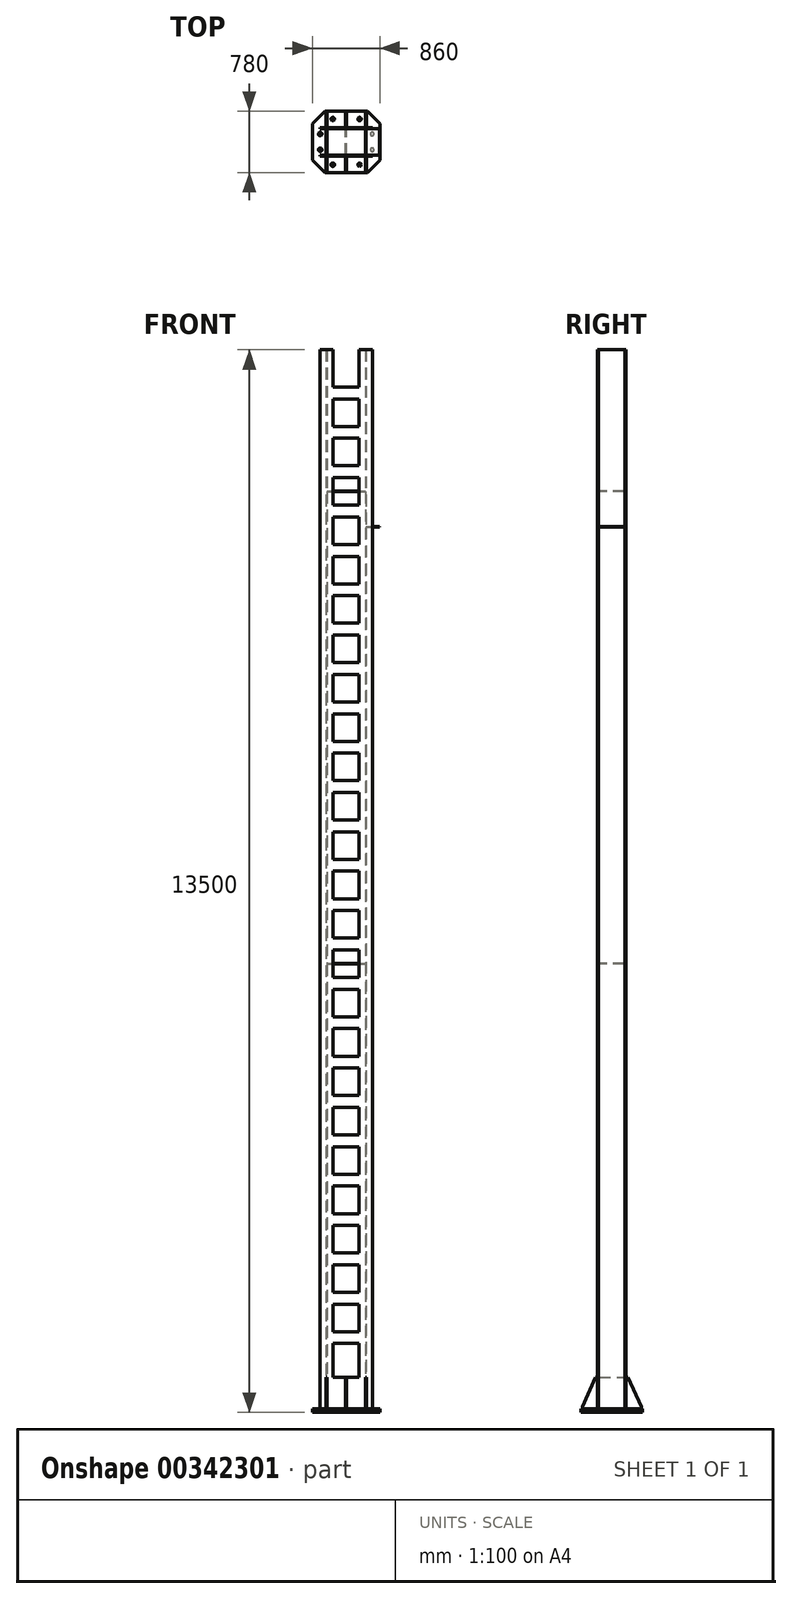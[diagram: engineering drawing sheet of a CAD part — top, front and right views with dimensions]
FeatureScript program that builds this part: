
annotation { "Feature Type Name" : "Feature", "Feature Type Description" : "" }
export const myFeature = defineFeature(function(context is Context, id is Id, definition is map)
    precondition{}
    {
        {
            var Q0;
            Q0=qCreatedBy(makeId("Top.planeOp"),FACE);
            var sketch = newSketch(context, id + "F0", { "sketchPlane" : qUnion([Q0])});
            skLineSegment(sketch, "E0", {"start": v(-335, 180) * mm, "end": v(335, 180) * mm});
            skLineSegment(sketch, "E1", {"start": v(335, 180) * mm, "end": v(335, 167.3) * mm});
            skLineSegment(sketch, "E2", {"start": v(335, 167.3) * mm, "end": v(254, 167.3) * mm});
            skLineSegment(sketch, "E3", {"start": v(254, 167.3) * mm, "end": v(254, -167.3) * mm});
            skLineSegment(sketch, "E4", {"start": v(254, -167.3) * mm, "end": v(335, -167.3) * mm});
            skLineSegment(sketch, "E5", {"start": v(335, -167.3) * mm, "end": v(335, -180) * mm});
            skLineSegment(sketch, "E6", {"start": v(335, -180) * mm, "end": v(-335, -180) * mm});
            skLineSegment(sketch, "E7", {"start": v(-335, -180) * mm, "end": v(-335, -167.3) * mm});
            skLineSegment(sketch, "E8", {"start": v(-335, -167.3) * mm, "end": v(-254, -167.3) * mm});
            skLineSegment(sketch, "E9", {"start": v(-254, -167.3) * mm, "end": v(-254, 167.3) * mm});
            skLineSegment(sketch, "E10", {"start": v(-254, 167.3) * mm, "end": v(-335, 167.3) * mm});
            skLineSegment(sketch, "E11", {"start": v(-335, 167.3) * mm, "end": v(-335, 180) * mm});
            skPoint(sketch, "E12.visualSharp", {"position": v(-254, 167.3) * mm});
            skPoint(sketch, "E13.visualSharp", {"position": v(254, 167.3) * mm});
            skPoint(sketch, "E14.visualSharp", {"position": v(254, -167.3) * mm});
            skPoint(sketch, "E15.visualSharp", {"position": v(-254, -167.3) * mm});
            skSolve(sketch);
        }
        {
            var Q0;
            Q0=qSketchRegion(id+"F0",true);
            extrude(context, id + "F1", {"entities" : qUnion([Q0]), "depth" : 13500 * mm});
        }
        {
            var Q0;
            Q0=makeQuery(id+"F1.opExtrude","CAP_FACE",FACE,{"disambiguationData":[OSD([sQuery(id+"F0.wireOp",EDGE,"E0"),sQuery(id+"F0.wireOp",EDGE,"E1"),sQuery(id+"F0.wireOp",EDGE,"E2"),sQuery(id+"F0.wireOp",EDGE,"E3"),sQuery(id+"F0.wireOp",EDGE,"E4"),sQuery(id+"F0.wireOp",EDGE,"E5"),sQuery(id+"F0.wireOp",EDGE,"E6"),sQuery(id+"F0.wireOp",EDGE,"E7"),sQuery(id+"F0.wireOp",EDGE,"E8"),sQuery(id+"F0.wireOp",EDGE,"E9"),sQuery(id+"F0.wireOp",EDGE,"E10"),sQuery(id+"F0.wireOp",EDGE,"E11"),sQuery(id+"F0.wireOp",EDGE,"E12.filletArc"),sQuery(id+"F0.wireOp",EDGE,"E13.filletArc"),sQuery(id+"F0.wireOp",EDGE,"E14.filletArc"),sQuery(id+"F0.wireOp",EDGE,"E15.filletArc")])],"isStart":true});
            var sketch = newSketch(context, id + "F2", { "sketchPlane" : qUnion([Q0])});
            skLineSegment(sketch, "E16.bottom", {"start": v(-246, 167.3) * mm, "end": v(246, 167.3) * mm});
            skLineSegment(sketch, "E16.top", {"start": v(-246, -167.3) * mm, "end": v(246, -167.3) * mm});
            skLineSegment(sketch, "E16.left", {"start": v(-246, 167.3) * mm, "end": v(-246, -167.3) * mm});
            skLineSegment(sketch, "E16.right", {"start": v(246, 167.3) * mm, "end": v(246, -167.3) * mm});
            skPoint(sketch, "E17.visualSharp", {"position": v(-246, 167.3) * mm});
            skPoint(sketch, "E18.visualSharp", {"position": v(246, 167.3) * mm});
            skPoint(sketch, "E19.visualSharp", {"position": v(246, -167.3) * mm});
            skPoint(sketch, "E20.visualSharp", {"position": v(-246, -167.3) * mm});
            skLineSegment(sketch, "E21", {"start": v(-272.18, 0) * mm, "end": v(268.26, 0) * mm, "construction": true});
            skLineSegment(sketch, "E22", {"start": v(0, 198) * mm, "end": v(0, -205.98) * mm, "construction": true});
            skSolve(sketch);
        }
        {
            var Q0;
            Q0=qSketchRegion(id+"F2",true);
            extrude(context, id + "F3", {"entities" : qUnion([Q0]), "operationType" : NewBodyOperationType.REMOVE, "endBound" : BoundingType.THROUGH_ALL, "oppositeDirection" : true, "depth" : 25.4 * mm});
        }
        {
            var Q0;
            Q0=makeQuery(id+"F1.opExtrude","SWEPT_FACE",FACE,{"disambiguationData":[OSD([sQuery(id+"F0.wireOp",EDGE,"E6")])]});
            var sketch = newSketch(context, id + "F4", { "sketchPlane" : qUnion([Q0])});
            skLineSegment(sketch, "E23.bottom", {"start": v(-165, 1375) * mm, "end": v(165, 1375) * mm});
            skLineSegment(sketch, "E23.top", {"start": v(-165, 1025) * mm, "end": v(165, 1025) * mm});
            skLineSegment(sketch, "E23.left", {"start": v(-165, 1375) * mm, "end": v(-165, 1025) * mm});
            skLineSegment(sketch, "E23.right", {"start": v(165, 1375) * mm, "end": v(165, 1025) * mm});
            skLineSegment(sketch, "E24", {"start": v(0, -2627.58) * mm, "end": v(0, 406140.36) * mm, "construction": true});
            skLineSegment(sketch, "E25.0.1.0", {"start": v(-165, 1875) * mm, "end": v(165, 1875) * mm});
            skLineSegment(sketch, "E25.0.1.1", {"start": v(-165, 1525) * mm, "end": v(165, 1525) * mm});
            skLineSegment(sketch, "E25.0.1.2", {"start": v(-165, 1875) * mm, "end": v(-165, 1525) * mm});
            skLineSegment(sketch, "E25.0.1.3", {"start": v(165, 1875) * mm, "end": v(165, 1525) * mm});
            skLineSegment(sketch, "E25.0.2.0", {"start": v(-165, 2375) * mm, "end": v(165, 2375) * mm});
            skLineSegment(sketch, "E25.0.2.1", {"start": v(-165, 2025) * mm, "end": v(165, 2025) * mm});
            skLineSegment(sketch, "E25.0.2.2", {"start": v(-165, 2375) * mm, "end": v(-165, 2025) * mm});
            skLineSegment(sketch, "E25.0.2.3", {"start": v(165, 2375) * mm, "end": v(165, 2025) * mm});
            skLineSegment(sketch, "E25.0.3.0", {"start": v(-165, 2875) * mm, "end": v(165, 2875) * mm});
            skLineSegment(sketch, "E25.0.3.1", {"start": v(-165, 2525) * mm, "end": v(165, 2525) * mm});
            skLineSegment(sketch, "E25.0.3.2", {"start": v(-165, 2875) * mm, "end": v(-165, 2525) * mm});
            skLineSegment(sketch, "E25.0.3.3", {"start": v(165, 2875) * mm, "end": v(165, 2525) * mm});
            skLineSegment(sketch, "E25.0.4.0", {"start": v(-165, 3375) * mm, "end": v(165, 3375) * mm});
            skLineSegment(sketch, "E25.0.4.1", {"start": v(-165, 3025) * mm, "end": v(165, 3025) * mm});
            skLineSegment(sketch, "E25.0.4.2", {"start": v(-165, 3375) * mm, "end": v(-165, 3025) * mm});
            skLineSegment(sketch, "E25.0.4.3", {"start": v(165, 3375) * mm, "end": v(165, 3025) * mm});
            skLineSegment(sketch, "E25.0.5.0", {"start": v(-165, 3875) * mm, "end": v(165, 3875) * mm});
            skLineSegment(sketch, "E25.0.5.1", {"start": v(-165, 3525) * mm, "end": v(165, 3525) * mm});
            skLineSegment(sketch, "E25.0.5.2", {"start": v(-165, 3875) * mm, "end": v(-165, 3525) * mm});
            skLineSegment(sketch, "E25.0.5.3", {"start": v(165, 3875) * mm, "end": v(165, 3525) * mm});
            skLineSegment(sketch, "E25.0.6.0", {"start": v(-165, 4375) * mm, "end": v(165, 4375) * mm});
            skLineSegment(sketch, "E25.0.6.1", {"start": v(-165, 4025) * mm, "end": v(165, 4025) * mm});
            skLineSegment(sketch, "E25.0.6.2", {"start": v(-165, 4375) * mm, "end": v(-165, 4025) * mm});
            skLineSegment(sketch, "E25.0.6.3", {"start": v(165, 4375) * mm, "end": v(165, 4025) * mm});
            skLineSegment(sketch, "E25.0.7.0", {"start": v(-165, 4875) * mm, "end": v(165, 4875) * mm});
            skLineSegment(sketch, "E25.0.7.1", {"start": v(-165, 4525) * mm, "end": v(165, 4525) * mm});
            skLineSegment(sketch, "E25.0.7.2", {"start": v(-165, 4875) * mm, "end": v(-165, 4525) * mm});
            skLineSegment(sketch, "E25.0.7.3", {"start": v(165, 4875) * mm, "end": v(165, 4525) * mm});
            skLineSegment(sketch, "E25.0.8.0", {"start": v(-165, 5375) * mm, "end": v(165, 5375) * mm});
            skLineSegment(sketch, "E25.0.8.1", {"start": v(-165, 5025) * mm, "end": v(165, 5025) * mm});
            skLineSegment(sketch, "E25.0.8.2", {"start": v(-165, 5375) * mm, "end": v(-165, 5025) * mm});
            skLineSegment(sketch, "E25.0.8.3", {"start": v(165, 5375) * mm, "end": v(165, 5025) * mm});
            skLineSegment(sketch, "E25.0.9.0", {"start": v(-165, 5875) * mm, "end": v(165, 5875) * mm});
            skLineSegment(sketch, "E25.0.9.1", {"start": v(-165, 5525) * mm, "end": v(165, 5525) * mm});
            skLineSegment(sketch, "E25.0.9.2", {"start": v(-165, 5875) * mm, "end": v(-165, 5525) * mm});
            skLineSegment(sketch, "E25.0.9.3", {"start": v(165, 5875) * mm, "end": v(165, 5525) * mm});
            skLineSegment(sketch, "E25.0.10.0", {"start": v(-165, 6375) * mm, "end": v(165, 6375) * mm});
            skLineSegment(sketch, "E25.0.10.1", {"start": v(-165, 6025) * mm, "end": v(165, 6025) * mm});
            skLineSegment(sketch, "E25.0.10.2", {"start": v(-165, 6375) * mm, "end": v(-165, 6025) * mm});
            skLineSegment(sketch, "E25.0.10.3", {"start": v(165, 6375) * mm, "end": v(165, 6025) * mm});
            skLineSegment(sketch, "E25.0.11.0", {"start": v(-165, 6875) * mm, "end": v(165, 6875) * mm});
            skLineSegment(sketch, "E25.0.11.1", {"start": v(-165, 6525) * mm, "end": v(165, 6525) * mm});
            skLineSegment(sketch, "E25.0.11.2", {"start": v(-165, 6875) * mm, "end": v(-165, 6525) * mm});
            skLineSegment(sketch, "E25.0.11.3", {"start": v(165, 6875) * mm, "end": v(165, 6525) * mm});
            skLineSegment(sketch, "E25.0.12.0", {"start": v(-165, 7375) * mm, "end": v(165, 7375) * mm});
            skLineSegment(sketch, "E25.0.12.1", {"start": v(-165, 7025) * mm, "end": v(165, 7025) * mm});
            skLineSegment(sketch, "E25.0.12.2", {"start": v(-165, 7375) * mm, "end": v(-165, 7025) * mm});
            skLineSegment(sketch, "E25.0.12.3", {"start": v(165, 7375) * mm, "end": v(165, 7025) * mm});
            skLineSegment(sketch, "E25.0.13.0", {"start": v(-165, 7875) * mm, "end": v(165, 7875) * mm});
            skLineSegment(sketch, "E25.0.13.1", {"start": v(-165, 7525) * mm, "end": v(165, 7525) * mm});
            skLineSegment(sketch, "E25.0.13.2", {"start": v(-165, 7875) * mm, "end": v(-165, 7525) * mm});
            skLineSegment(sketch, "E25.0.13.3", {"start": v(165, 7875) * mm, "end": v(165, 7525) * mm});
            skLineSegment(sketch, "E25.0.14.0", {"start": v(-165, 8375) * mm, "end": v(165, 8375) * mm});
            skLineSegment(sketch, "E25.0.14.1", {"start": v(-165, 8025) * mm, "end": v(165, 8025) * mm});
            skLineSegment(sketch, "E25.0.14.2", {"start": v(-165, 8375) * mm, "end": v(-165, 8025) * mm});
            skLineSegment(sketch, "E25.0.14.3", {"start": v(165, 8375) * mm, "end": v(165, 8025) * mm});
            skLineSegment(sketch, "E25.0.15.0", {"start": v(-165, 8875) * mm, "end": v(165, 8875) * mm});
            skLineSegment(sketch, "E25.0.15.1", {"start": v(-165, 8525) * mm, "end": v(165, 8525) * mm});
            skLineSegment(sketch, "E25.0.15.2", {"start": v(-165, 8875) * mm, "end": v(-165, 8525) * mm});
            skLineSegment(sketch, "E25.0.15.3", {"start": v(165, 8875) * mm, "end": v(165, 8525) * mm});
            skLineSegment(sketch, "E25.0.16.0", {"start": v(-165, 9375) * mm, "end": v(165, 9375) * mm});
            skLineSegment(sketch, "E25.0.16.1", {"start": v(-165, 9025) * mm, "end": v(165, 9025) * mm});
            skLineSegment(sketch, "E25.0.16.2", {"start": v(-165, 9375) * mm, "end": v(-165, 9025) * mm});
            skLineSegment(sketch, "E25.0.16.3", {"start": v(165, 9375) * mm, "end": v(165, 9025) * mm});
            skLineSegment(sketch, "E25.0.17.0", {"start": v(-165, 9875) * mm, "end": v(165, 9875) * mm});
            skLineSegment(sketch, "E25.0.17.1", {"start": v(-165, 9525) * mm, "end": v(165, 9525) * mm});
            skLineSegment(sketch, "E25.0.17.2", {"start": v(-165, 9875) * mm, "end": v(-165, 9525) * mm});
            skLineSegment(sketch, "E25.0.17.3", {"start": v(165, 9875) * mm, "end": v(165, 9525) * mm});
            skLineSegment(sketch, "E25.0.18.0", {"start": v(-165, 10375) * mm, "end": v(165, 10375) * mm});
            skLineSegment(sketch, "E25.0.18.1", {"start": v(-165, 10025) * mm, "end": v(165, 10025) * mm});
            skLineSegment(sketch, "E25.0.18.2", {"start": v(-165, 10375) * mm, "end": v(-165, 10025) * mm});
            skLineSegment(sketch, "E25.0.18.3", {"start": v(165, 10375) * mm, "end": v(165, 10025) * mm});
            skLineSegment(sketch, "E25.0.19.0", {"start": v(-165, 10875) * mm, "end": v(165, 10875) * mm});
            skLineSegment(sketch, "E25.0.19.1", {"start": v(-165, 10525) * mm, "end": v(165, 10525) * mm});
            skLineSegment(sketch, "E25.0.19.2", {"start": v(-165, 10875) * mm, "end": v(-165, 10525) * mm});
            skLineSegment(sketch, "E25.0.19.3", {"start": v(165, 10875) * mm, "end": v(165, 10525) * mm});
            skLineSegment(sketch, "E25.0.20.0", {"start": v(-165, 11375) * mm, "end": v(165, 11375) * mm});
            skLineSegment(sketch, "E25.0.20.1", {"start": v(-165, 11025) * mm, "end": v(165, 11025) * mm});
            skLineSegment(sketch, "E25.0.20.2", {"start": v(-165, 11375) * mm, "end": v(-165, 11025) * mm});
            skLineSegment(sketch, "E25.0.20.3", {"start": v(165, 11375) * mm, "end": v(165, 11025) * mm});
            skLineSegment(sketch, "E25.0.21.0", {"start": v(-165, 11875) * mm, "end": v(165, 11875) * mm});
            skLineSegment(sketch, "E25.0.21.1", {"start": v(-165, 11525) * mm, "end": v(165, 11525) * mm});
            skLineSegment(sketch, "E25.0.21.2", {"start": v(-165, 11875) * mm, "end": v(-165, 11525) * mm});
            skLineSegment(sketch, "E25.0.21.3", {"start": v(165, 11875) * mm, "end": v(165, 11525) * mm});
            skLineSegment(sketch, "E25.0.22.0", {"start": v(-165, 12375) * mm, "end": v(165, 12375) * mm});
            skLineSegment(sketch, "E25.0.22.1", {"start": v(-165, 12025) * mm, "end": v(165, 12025) * mm});
            skLineSegment(sketch, "E25.0.22.2", {"start": v(-165, 12375) * mm, "end": v(-165, 12025) * mm});
            skLineSegment(sketch, "E25.0.22.3", {"start": v(165, 12375) * mm, "end": v(165, 12025) * mm});
            skLineSegment(sketch, "E25.0.23.0", {"start": v(-165, 12875) * mm, "end": v(165, 12875) * mm});
            skLineSegment(sketch, "E25.0.23.1", {"start": v(-165, 12525) * mm, "end": v(165, 12525) * mm});
            skLineSegment(sketch, "E25.0.23.2", {"start": v(-165, 12875) * mm, "end": v(-165, 12525) * mm});
            skLineSegment(sketch, "E25.0.23.3", {"start": v(165, 12875) * mm, "end": v(165, 12525) * mm});
            skLineSegment(sketch, "E25.1.1.0", {"start": v(-165, 1875) * mm, "end": v(165, 1875) * mm});
            skLineSegment(sketch, "E25.1.1.1", {"start": v(-165, 1525) * mm, "end": v(165, 1525) * mm});
            skLineSegment(sketch, "E25.1.1.2", {"start": v(-165, 1875) * mm, "end": v(-165, 1525) * mm});
            skLineSegment(sketch, "E25.1.1.3", {"start": v(165, 1875) * mm, "end": v(165, 1525) * mm});
            skLineSegment(sketch, "E25.1.2.0", {"start": v(-165, 2375) * mm, "end": v(165, 2375) * mm});
            skLineSegment(sketch, "E25.1.2.1", {"start": v(-165, 2025) * mm, "end": v(165, 2025) * mm});
            skLineSegment(sketch, "E25.1.2.2", {"start": v(-165, 2375) * mm, "end": v(-165, 2025) * mm});
            skLineSegment(sketch, "E25.1.2.3", {"start": v(165, 2375) * mm, "end": v(165, 2025) * mm});
            skLineSegment(sketch, "E25.1.3.0", {"start": v(-165, 2875) * mm, "end": v(165, 2875) * mm});
            skLineSegment(sketch, "E25.1.3.1", {"start": v(-165, 2525) * mm, "end": v(165, 2525) * mm});
            skLineSegment(sketch, "E25.1.3.2", {"start": v(-165, 2875) * mm, "end": v(-165, 2525) * mm});
            skLineSegment(sketch, "E25.1.3.3", {"start": v(165, 2875) * mm, "end": v(165, 2525) * mm});
            skLineSegment(sketch, "E25.1.4.0", {"start": v(-165, 3375) * mm, "end": v(165, 3375) * mm});
            skLineSegment(sketch, "E25.1.4.1", {"start": v(-165, 3025) * mm, "end": v(165, 3025) * mm});
            skLineSegment(sketch, "E25.1.4.2", {"start": v(-165, 3375) * mm, "end": v(-165, 3025) * mm});
            skLineSegment(sketch, "E25.1.4.3", {"start": v(165, 3375) * mm, "end": v(165, 3025) * mm});
            skLineSegment(sketch, "E25.1.5.0", {"start": v(-165, 3875) * mm, "end": v(165, 3875) * mm});
            skLineSegment(sketch, "E25.1.5.1", {"start": v(-165, 3525) * mm, "end": v(165, 3525) * mm});
            skLineSegment(sketch, "E25.1.5.2", {"start": v(-165, 3875) * mm, "end": v(-165, 3525) * mm});
            skLineSegment(sketch, "E25.1.5.3", {"start": v(165, 3875) * mm, "end": v(165, 3525) * mm});
            skLineSegment(sketch, "E25.1.6.0", {"start": v(-165, 4375) * mm, "end": v(165, 4375) * mm});
            skLineSegment(sketch, "E25.1.6.1", {"start": v(-165, 4025) * mm, "end": v(165, 4025) * mm});
            skLineSegment(sketch, "E25.1.6.2", {"start": v(-165, 4375) * mm, "end": v(-165, 4025) * mm});
            skLineSegment(sketch, "E25.1.6.3", {"start": v(165, 4375) * mm, "end": v(165, 4025) * mm});
            skLineSegment(sketch, "E25.1.7.0", {"start": v(-165, 4875) * mm, "end": v(165, 4875) * mm});
            skLineSegment(sketch, "E25.1.7.1", {"start": v(-165, 4525) * mm, "end": v(165, 4525) * mm});
            skLineSegment(sketch, "E25.1.7.2", {"start": v(-165, 4875) * mm, "end": v(-165, 4525) * mm});
            skLineSegment(sketch, "E25.1.7.3", {"start": v(165, 4875) * mm, "end": v(165, 4525) * mm});
            skLineSegment(sketch, "E25.1.8.0", {"start": v(-165, 5375) * mm, "end": v(165, 5375) * mm});
            skLineSegment(sketch, "E25.1.8.1", {"start": v(-165, 5025) * mm, "end": v(165, 5025) * mm});
            skLineSegment(sketch, "E25.1.8.2", {"start": v(-165, 5375) * mm, "end": v(-165, 5025) * mm});
            skLineSegment(sketch, "E25.1.8.3", {"start": v(165, 5375) * mm, "end": v(165, 5025) * mm});
            skLineSegment(sketch, "E25.1.9.0", {"start": v(-165, 5875) * mm, "end": v(165, 5875) * mm});
            skLineSegment(sketch, "E25.1.9.1", {"start": v(-165, 5525) * mm, "end": v(165, 5525) * mm});
            skLineSegment(sketch, "E25.1.9.2", {"start": v(-165, 5875) * mm, "end": v(-165, 5525) * mm});
            skLineSegment(sketch, "E25.1.9.3", {"start": v(165, 5875) * mm, "end": v(165, 5525) * mm});
            skLineSegment(sketch, "E25.1.10.0", {"start": v(-165, 6375) * mm, "end": v(165, 6375) * mm});
            skLineSegment(sketch, "E25.1.10.1", {"start": v(-165, 6025) * mm, "end": v(165, 6025) * mm});
            skLineSegment(sketch, "E25.1.10.2", {"start": v(-165, 6375) * mm, "end": v(-165, 6025) * mm});
            skLineSegment(sketch, "E25.1.10.3", {"start": v(165, 6375) * mm, "end": v(165, 6025) * mm});
            skLineSegment(sketch, "E25.1.11.0", {"start": v(-165, 6875) * mm, "end": v(165, 6875) * mm});
            skLineSegment(sketch, "E25.1.11.1", {"start": v(-165, 6525) * mm, "end": v(165, 6525) * mm});
            skLineSegment(sketch, "E25.1.11.2", {"start": v(-165, 6875) * mm, "end": v(-165, 6525) * mm});
            skLineSegment(sketch, "E25.1.11.3", {"start": v(165, 6875) * mm, "end": v(165, 6525) * mm});
            skLineSegment(sketch, "E25.1.12.0", {"start": v(-165, 7375) * mm, "end": v(165, 7375) * mm});
            skLineSegment(sketch, "E25.1.12.1", {"start": v(-165, 7025) * mm, "end": v(165, 7025) * mm});
            skLineSegment(sketch, "E25.1.12.2", {"start": v(-165, 7375) * mm, "end": v(-165, 7025) * mm});
            skLineSegment(sketch, "E25.1.12.3", {"start": v(165, 7375) * mm, "end": v(165, 7025) * mm});
            skLineSegment(sketch, "E25.1.13.0", {"start": v(-165, 7875) * mm, "end": v(165, 7875) * mm});
            skLineSegment(sketch, "E25.1.13.1", {"start": v(-165, 7525) * mm, "end": v(165, 7525) * mm});
            skLineSegment(sketch, "E25.1.13.2", {"start": v(-165, 7875) * mm, "end": v(-165, 7525) * mm});
            skLineSegment(sketch, "E25.1.13.3", {"start": v(165, 7875) * mm, "end": v(165, 7525) * mm});
            skLineSegment(sketch, "E25.1.14.0", {"start": v(-165, 8375) * mm, "end": v(165, 8375) * mm});
            skLineSegment(sketch, "E25.1.14.1", {"start": v(-165, 8025) * mm, "end": v(165, 8025) * mm});
            skLineSegment(sketch, "E25.1.14.2", {"start": v(-165, 8375) * mm, "end": v(-165, 8025) * mm});
            skLineSegment(sketch, "E25.1.14.3", {"start": v(165, 8375) * mm, "end": v(165, 8025) * mm});
            skLineSegment(sketch, "E25.1.15.0", {"start": v(-165, 8875) * mm, "end": v(165, 8875) * mm});
            skLineSegment(sketch, "E25.1.15.1", {"start": v(-165, 8525) * mm, "end": v(165, 8525) * mm});
            skLineSegment(sketch, "E25.1.15.2", {"start": v(-165, 8875) * mm, "end": v(-165, 8525) * mm});
            skLineSegment(sketch, "E25.1.15.3", {"start": v(165, 8875) * mm, "end": v(165, 8525) * mm});
            skLineSegment(sketch, "E25.1.16.0", {"start": v(-165, 9375) * mm, "end": v(165, 9375) * mm});
            skLineSegment(sketch, "E25.1.16.1", {"start": v(-165, 9025) * mm, "end": v(165, 9025) * mm});
            skLineSegment(sketch, "E25.1.16.2", {"start": v(-165, 9375) * mm, "end": v(-165, 9025) * mm});
            skLineSegment(sketch, "E25.1.16.3", {"start": v(165, 9375) * mm, "end": v(165, 9025) * mm});
            skLineSegment(sketch, "E25.1.17.0", {"start": v(-165, 9875) * mm, "end": v(165, 9875) * mm});
            skLineSegment(sketch, "E25.1.17.1", {"start": v(-165, 9525) * mm, "end": v(165, 9525) * mm});
            skLineSegment(sketch, "E25.1.17.2", {"start": v(-165, 9875) * mm, "end": v(-165, 9525) * mm});
            skLineSegment(sketch, "E25.1.17.3", {"start": v(165, 9875) * mm, "end": v(165, 9525) * mm});
            skLineSegment(sketch, "E25.1.18.0", {"start": v(-165, 10375) * mm, "end": v(165, 10375) * mm});
            skLineSegment(sketch, "E25.1.18.1", {"start": v(-165, 10025) * mm, "end": v(165, 10025) * mm});
            skLineSegment(sketch, "E25.1.18.2", {"start": v(-165, 10375) * mm, "end": v(-165, 10025) * mm});
            skLineSegment(sketch, "E25.1.18.3", {"start": v(165, 10375) * mm, "end": v(165, 10025) * mm});
            skLineSegment(sketch, "E25.1.19.0", {"start": v(-165, 10875) * mm, "end": v(165, 10875) * mm});
            skLineSegment(sketch, "E25.1.19.1", {"start": v(-165, 10525) * mm, "end": v(165, 10525) * mm});
            skLineSegment(sketch, "E25.1.19.2", {"start": v(-165, 10875) * mm, "end": v(-165, 10525) * mm});
            skLineSegment(sketch, "E25.1.19.3", {"start": v(165, 10875) * mm, "end": v(165, 10525) * mm});
            skLineSegment(sketch, "E25.1.20.0", {"start": v(-165, 11375) * mm, "end": v(165, 11375) * mm});
            skLineSegment(sketch, "E25.1.20.1", {"start": v(-165, 11025) * mm, "end": v(165, 11025) * mm});
            skLineSegment(sketch, "E25.1.20.2", {"start": v(-165, 11375) * mm, "end": v(-165, 11025) * mm});
            skLineSegment(sketch, "E25.1.20.3", {"start": v(165, 11375) * mm, "end": v(165, 11025) * mm});
            skLineSegment(sketch, "E25.1.21.0", {"start": v(-165, 11875) * mm, "end": v(165, 11875) * mm});
            skLineSegment(sketch, "E25.1.21.1", {"start": v(-165, 11525) * mm, "end": v(165, 11525) * mm});
            skLineSegment(sketch, "E25.1.21.2", {"start": v(-165, 11875) * mm, "end": v(-165, 11525) * mm});
            skLineSegment(sketch, "E25.1.21.3", {"start": v(165, 11875) * mm, "end": v(165, 11525) * mm});
            skLineSegment(sketch, "E25.1.22.0", {"start": v(-165, 12375) * mm, "end": v(165, 12375) * mm});
            skLineSegment(sketch, "E25.1.22.1", {"start": v(-165, 12025) * mm, "end": v(165, 12025) * mm});
            skLineSegment(sketch, "E25.1.22.2", {"start": v(-165, 12375) * mm, "end": v(-165, 12025) * mm});
            skLineSegment(sketch, "E25.1.22.3", {"start": v(165, 12375) * mm, "end": v(165, 12025) * mm});
            skLineSegment(sketch, "E25.1.23.0", {"start": v(-165, 12875) * mm, "end": v(165, 12875) * mm});
            skLineSegment(sketch, "E25.1.23.1", {"start": v(-165, 12525) * mm, "end": v(165, 12525) * mm});
            skLineSegment(sketch, "E25.1.23.2", {"start": v(-165, 12875) * mm, "end": v(-165, 12525) * mm});
            skLineSegment(sketch, "E25.1.23.3", {"start": v(165, 12875) * mm, "end": v(165, 12525) * mm});
            skLineSegment(sketch, "E25.2.1.0", {"start": v(-165, 1875) * mm, "end": v(165, 1875) * mm});
            skLineSegment(sketch, "E25.2.1.1", {"start": v(-165, 1525) * mm, "end": v(165, 1525) * mm});
            skLineSegment(sketch, "E25.2.1.2", {"start": v(-165, 1875) * mm, "end": v(-165, 1525) * mm});
            skLineSegment(sketch, "E25.2.1.3", {"start": v(165, 1875) * mm, "end": v(165, 1525) * mm});
            skLineSegment(sketch, "E25.2.2.0", {"start": v(-165, 2375) * mm, "end": v(165, 2375) * mm});
            skLineSegment(sketch, "E25.2.2.1", {"start": v(-165, 2025) * mm, "end": v(165, 2025) * mm});
            skLineSegment(sketch, "E25.2.2.2", {"start": v(-165, 2375) * mm, "end": v(-165, 2025) * mm});
            skLineSegment(sketch, "E25.2.2.3", {"start": v(165, 2375) * mm, "end": v(165, 2025) * mm});
            skLineSegment(sketch, "E25.2.3.0", {"start": v(-165, 2875) * mm, "end": v(165, 2875) * mm});
            skLineSegment(sketch, "E25.2.3.1", {"start": v(-165, 2525) * mm, "end": v(165, 2525) * mm});
            skLineSegment(sketch, "E25.2.3.2", {"start": v(-165, 2875) * mm, "end": v(-165, 2525) * mm});
            skLineSegment(sketch, "E25.2.3.3", {"start": v(165, 2875) * mm, "end": v(165, 2525) * mm});
            skLineSegment(sketch, "E25.2.4.0", {"start": v(-165, 3375) * mm, "end": v(165, 3375) * mm});
            skLineSegment(sketch, "E25.2.4.1", {"start": v(-165, 3025) * mm, "end": v(165, 3025) * mm});
            skLineSegment(sketch, "E25.2.4.2", {"start": v(-165, 3375) * mm, "end": v(-165, 3025) * mm});
            skLineSegment(sketch, "E25.2.4.3", {"start": v(165, 3375) * mm, "end": v(165, 3025) * mm});
            skLineSegment(sketch, "E25.2.5.0", {"start": v(-165, 3875) * mm, "end": v(165, 3875) * mm});
            skLineSegment(sketch, "E25.2.5.1", {"start": v(-165, 3525) * mm, "end": v(165, 3525) * mm});
            skLineSegment(sketch, "E25.2.5.2", {"start": v(-165, 3875) * mm, "end": v(-165, 3525) * mm});
            skLineSegment(sketch, "E25.2.5.3", {"start": v(165, 3875) * mm, "end": v(165, 3525) * mm});
            skLineSegment(sketch, "E25.2.6.0", {"start": v(-165, 4375) * mm, "end": v(165, 4375) * mm});
            skLineSegment(sketch, "E25.2.6.1", {"start": v(-165, 4025) * mm, "end": v(165, 4025) * mm});
            skLineSegment(sketch, "E25.2.6.2", {"start": v(-165, 4375) * mm, "end": v(-165, 4025) * mm});
            skLineSegment(sketch, "E25.2.6.3", {"start": v(165, 4375) * mm, "end": v(165, 4025) * mm});
            skLineSegment(sketch, "E25.2.7.0", {"start": v(-165, 4875) * mm, "end": v(165, 4875) * mm});
            skLineSegment(sketch, "E25.2.7.1", {"start": v(-165, 4525) * mm, "end": v(165, 4525) * mm});
            skLineSegment(sketch, "E25.2.7.2", {"start": v(-165, 4875) * mm, "end": v(-165, 4525) * mm});
            skLineSegment(sketch, "E25.2.7.3", {"start": v(165, 4875) * mm, "end": v(165, 4525) * mm});
            skLineSegment(sketch, "E25.2.8.0", {"start": v(-165, 5375) * mm, "end": v(165, 5375) * mm});
            skLineSegment(sketch, "E25.2.8.1", {"start": v(-165, 5025) * mm, "end": v(165, 5025) * mm});
            skLineSegment(sketch, "E25.2.8.2", {"start": v(-165, 5375) * mm, "end": v(-165, 5025) * mm});
            skLineSegment(sketch, "E25.2.8.3", {"start": v(165, 5375) * mm, "end": v(165, 5025) * mm});
            skLineSegment(sketch, "E25.2.9.0", {"start": v(-165, 5875) * mm, "end": v(165, 5875) * mm});
            skLineSegment(sketch, "E25.2.9.1", {"start": v(-165, 5525) * mm, "end": v(165, 5525) * mm});
            skLineSegment(sketch, "E25.2.9.2", {"start": v(-165, 5875) * mm, "end": v(-165, 5525) * mm});
            skLineSegment(sketch, "E25.2.9.3", {"start": v(165, 5875) * mm, "end": v(165, 5525) * mm});
            skLineSegment(sketch, "E25.2.10.0", {"start": v(-165, 6375) * mm, "end": v(165, 6375) * mm});
            skLineSegment(sketch, "E25.2.10.1", {"start": v(-165, 6025) * mm, "end": v(165, 6025) * mm});
            skLineSegment(sketch, "E25.2.10.2", {"start": v(-165, 6375) * mm, "end": v(-165, 6025) * mm});
            skLineSegment(sketch, "E25.2.10.3", {"start": v(165, 6375) * mm, "end": v(165, 6025) * mm});
            skLineSegment(sketch, "E25.2.11.0", {"start": v(-165, 6875) * mm, "end": v(165, 6875) * mm});
            skLineSegment(sketch, "E25.2.11.1", {"start": v(-165, 6525) * mm, "end": v(165, 6525) * mm});
            skLineSegment(sketch, "E25.2.11.2", {"start": v(-165, 6875) * mm, "end": v(-165, 6525) * mm});
            skLineSegment(sketch, "E25.2.11.3", {"start": v(165, 6875) * mm, "end": v(165, 6525) * mm});
            skLineSegment(sketch, "E25.2.12.0", {"start": v(-165, 7375) * mm, "end": v(165, 7375) * mm});
            skLineSegment(sketch, "E25.2.12.1", {"start": v(-165, 7025) * mm, "end": v(165, 7025) * mm});
            skLineSegment(sketch, "E25.2.12.2", {"start": v(-165, 7375) * mm, "end": v(-165, 7025) * mm});
            skLineSegment(sketch, "E25.2.12.3", {"start": v(165, 7375) * mm, "end": v(165, 7025) * mm});
            skLineSegment(sketch, "E25.2.13.0", {"start": v(-165, 7875) * mm, "end": v(165, 7875) * mm});
            skLineSegment(sketch, "E25.2.13.1", {"start": v(-165, 7525) * mm, "end": v(165, 7525) * mm});
            skLineSegment(sketch, "E25.2.13.2", {"start": v(-165, 7875) * mm, "end": v(-165, 7525) * mm});
            skLineSegment(sketch, "E25.2.13.3", {"start": v(165, 7875) * mm, "end": v(165, 7525) * mm});
            skLineSegment(sketch, "E25.2.14.0", {"start": v(-165, 8375) * mm, "end": v(165, 8375) * mm});
            skLineSegment(sketch, "E25.2.14.1", {"start": v(-165, 8025) * mm, "end": v(165, 8025) * mm});
            skLineSegment(sketch, "E25.2.14.2", {"start": v(-165, 8375) * mm, "end": v(-165, 8025) * mm});
            skLineSegment(sketch, "E25.2.14.3", {"start": v(165, 8375) * mm, "end": v(165, 8025) * mm});
            skLineSegment(sketch, "E25.2.15.0", {"start": v(-165, 8875) * mm, "end": v(165, 8875) * mm});
            skLineSegment(sketch, "E25.2.15.1", {"start": v(-165, 8525) * mm, "end": v(165, 8525) * mm});
            skLineSegment(sketch, "E25.2.15.2", {"start": v(-165, 8875) * mm, "end": v(-165, 8525) * mm});
            skLineSegment(sketch, "E25.2.15.3", {"start": v(165, 8875) * mm, "end": v(165, 8525) * mm});
            skLineSegment(sketch, "E25.2.16.0", {"start": v(-165, 9375) * mm, "end": v(165, 9375) * mm});
            skLineSegment(sketch, "E25.2.16.1", {"start": v(-165, 9025) * mm, "end": v(165, 9025) * mm});
            skLineSegment(sketch, "E25.2.16.2", {"start": v(-165, 9375) * mm, "end": v(-165, 9025) * mm});
            skLineSegment(sketch, "E25.2.16.3", {"start": v(165, 9375) * mm, "end": v(165, 9025) * mm});
            skLineSegment(sketch, "E25.2.17.0", {"start": v(-165, 9875) * mm, "end": v(165, 9875) * mm});
            skLineSegment(sketch, "E25.2.17.1", {"start": v(-165, 9525) * mm, "end": v(165, 9525) * mm});
            skLineSegment(sketch, "E25.2.17.2", {"start": v(-165, 9875) * mm, "end": v(-165, 9525) * mm});
            skLineSegment(sketch, "E25.2.17.3", {"start": v(165, 9875) * mm, "end": v(165, 9525) * mm});
            skLineSegment(sketch, "E25.2.18.0", {"start": v(-165, 10375) * mm, "end": v(165, 10375) * mm});
            skLineSegment(sketch, "E25.2.18.1", {"start": v(-165, 10025) * mm, "end": v(165, 10025) * mm});
            skLineSegment(sketch, "E25.2.18.2", {"start": v(-165, 10375) * mm, "end": v(-165, 10025) * mm});
            skLineSegment(sketch, "E25.2.18.3", {"start": v(165, 10375) * mm, "end": v(165, 10025) * mm});
            skLineSegment(sketch, "E25.2.19.0", {"start": v(-165, 10875) * mm, "end": v(165, 10875) * mm});
            skLineSegment(sketch, "E25.2.19.1", {"start": v(-165, 10525) * mm, "end": v(165, 10525) * mm});
            skLineSegment(sketch, "E25.2.19.2", {"start": v(-165, 10875) * mm, "end": v(-165, 10525) * mm});
            skLineSegment(sketch, "E25.2.19.3", {"start": v(165, 10875) * mm, "end": v(165, 10525) * mm});
            skLineSegment(sketch, "E25.2.20.0", {"start": v(-165, 11375) * mm, "end": v(165, 11375) * mm});
            skLineSegment(sketch, "E25.2.20.1", {"start": v(-165, 11025) * mm, "end": v(165, 11025) * mm});
            skLineSegment(sketch, "E25.2.20.2", {"start": v(-165, 11375) * mm, "end": v(-165, 11025) * mm});
            skLineSegment(sketch, "E25.2.20.3", {"start": v(165, 11375) * mm, "end": v(165, 11025) * mm});
            skLineSegment(sketch, "E25.2.21.0", {"start": v(-165, 11875) * mm, "end": v(165, 11875) * mm});
            skLineSegment(sketch, "E25.2.21.1", {"start": v(-165, 11525) * mm, "end": v(165, 11525) * mm});
            skLineSegment(sketch, "E25.2.21.2", {"start": v(-165, 11875) * mm, "end": v(-165, 11525) * mm});
            skLineSegment(sketch, "E25.2.21.3", {"start": v(165, 11875) * mm, "end": v(165, 11525) * mm});
            skLineSegment(sketch, "E25.2.22.0", {"start": v(-165, 12375) * mm, "end": v(165, 12375) * mm});
            skLineSegment(sketch, "E25.2.22.1", {"start": v(-165, 12025) * mm, "end": v(165, 12025) * mm});
            skLineSegment(sketch, "E25.2.22.2", {"start": v(-165, 12375) * mm, "end": v(-165, 12025) * mm});
            skLineSegment(sketch, "E25.2.22.3", {"start": v(165, 12375) * mm, "end": v(165, 12025) * mm});
            skLineSegment(sketch, "E25.2.23.0", {"start": v(-165, 12875) * mm, "end": v(165, 12875) * mm});
            skLineSegment(sketch, "E25.2.23.1", {"start": v(-165, 12525) * mm, "end": v(165, 12525) * mm});
            skLineSegment(sketch, "E25.2.23.2", {"start": v(-165, 12875) * mm, "end": v(-165, 12525) * mm});
            skLineSegment(sketch, "E25.2.23.3", {"start": v(165, 12875) * mm, "end": v(165, 12525) * mm});
            skLineSegment(sketch, "E25.direction1", {"start": v(-165, 1025) * mm, "end": v(-165, 1025) * mm});
            skLineSegment(sketch, "E25.direction2", {"start": v(-165, 1025) * mm, "end": v(-165, 1525) * mm, "construction": true});
            skLineSegment(sketch, "E26.bottom", {"start": v(-165, 13500) * mm, "end": v(165, 13500) * mm});
            skLineSegment(sketch, "E26.top", {"start": v(-165, 13025) * mm, "end": v(165, 13025) * mm});
            skLineSegment(sketch, "E26.left", {"start": v(-165, 13500) * mm, "end": v(-165, 13025) * mm});
            skLineSegment(sketch, "E26.right", {"start": v(165, 13500) * mm, "end": v(165, 13025) * mm});
            skLineSegment(sketch, "E27.bottom", {"start": v(-165, 875) * mm, "end": v(165, 875) * mm});
            skLineSegment(sketch, "E27.top", {"start": v(-165, 445) * mm, "end": v(165, 445) * mm});
            skLineSegment(sketch, "E27.left", {"start": v(-165, 875) * mm, "end": v(-165, 445) * mm});
            skLineSegment(sketch, "E27.right", {"start": v(165, 875) * mm, "end": v(165, 445) * mm});
            skSolve(sketch);
        }
        {
            var Q0;
            Q0=qSketchRegion(id+"F4",true);
            extrude(context, id + "F5", {"entities" : qUnion([Q0]), "operationType" : NewBodyOperationType.REMOVE, "endBound" : BoundingType.THROUGH_ALL, "oppositeDirection" : true, "depth" : 25.4 * mm});
        }
        {
            var Q0;
            Q0=qCreatedBy(makeId("Top.planeOp"),FACE);
            cPlane(context, id + "F6", {"entities" : qUnion([Q0]), "cplaneType" : CPlaneType.OFFSET, "offset" : 5700 * mm, "width" : 152.4 * mm, "height" : 152.4 * mm});
        }
        {
            var Q0;
            Q0=qCreatedBy(id+"F6.planeOp",FACE);
            var sketch = newSketch(context, id + "F7", { "sketchPlane" : qUnion([Q0])});
            skLineSegment(sketch, "E28", {"start": v(0, 198.37) * mm, "end": v(0, -212.1) * mm, "construction": true});
            skLineSegment(sketch, "E29", {"start": v(-268.37, 0) * mm, "end": v(278.72, 0) * mm, "construction": true});
            skLineSegment(sketch, "E30.bottom", {"start": v(-246, 167.3) * mm, "end": v(246, 167.3) * mm});
            skLineSegment(sketch, "E30.top", {"start": v(-246, -167.3) * mm, "end": v(246, -167.3) * mm});
            skLineSegment(sketch, "E30.left", {"start": v(-246, 167.3) * mm, "end": v(-246, -167.3) * mm});
            skLineSegment(sketch, "E30.right", {"start": v(246, 167.3) * mm, "end": v(246, -167.3) * mm});
            skPoint(sketch, "E31.visualSharp", {"position": v(-246, 167.3) * mm});
            skPoint(sketch, "E32.visualSharp", {"position": v(246, 167.3) * mm});
            skPoint(sketch, "E33.visualSharp", {"position": v(246, -167.3) * mm});
            skPoint(sketch, "E34.visualSharp", {"position": v(-246, -167.3) * mm});
            skSolve(sketch);
        }
        {
            var Q0;
            Q0=qSketchRegion(id+"F7",true);
            extrude(context, id + "F8", {"entities" : qUnion([Q0]), "operationType" : NewBodyOperationType.ADD, "endBound" : BoundingType.SYMMETRIC, "depth" : 6 * mm});
        }
        {
            var Q0;
            Q0=qCreatedBy(makeId("Top.planeOp"),FACE);
            cPlane(context, id + "F9", {"entities" : qUnion([Q0]), "cplaneType" : CPlaneType.OFFSET, "offset" : 11700 * mm, "width" : 152.4 * mm, "height" : 152.4 * mm});
        }
        {
            var Q0;
            Q0=qCreatedBy(id+"F9.planeOp",FACE);
            var sketch = newSketch(context, id + "F10", { "sketchPlane" : qUnion([Q0])});
            skLineSegment(sketch, "E35.bottom", {"start": v(-246, 167.3) * mm, "end": v(246, 167.3) * mm});
            skLineSegment(sketch, "E35.top", {"start": v(-246, -167.3) * mm, "end": v(246, -167.3) * mm});
            skLineSegment(sketch, "E35.left", {"start": v(-246, 167.3) * mm, "end": v(-246, -167.3) * mm});
            skLineSegment(sketch, "E35.right", {"start": v(246, 167.3) * mm, "end": v(246, -167.3) * mm});
            skLineSegment(sketch, "E36", {"start": v(-270.17, 0) * mm, "end": v(277.95, 0) * mm, "construction": true});
            skLineSegment(sketch, "E37", {"start": v(0, 205.82) * mm, "end": v(0, -214.2) * mm, "construction": true});
            skPoint(sketch, "E38.visualSharp", {"position": v(-246, 167.3) * mm});
            skPoint(sketch, "E39.visualSharp", {"position": v(246, 167.3) * mm});
            skPoint(sketch, "E40.visualSharp", {"position": v(246, -167.3) * mm});
            skPoint(sketch, "E41.visualSharp", {"position": v(-246, -167.3) * mm});
            skSolve(sketch);
        }
        {
            var Q0;
            Q0=qSketchRegion(id+"F10",true);
            extrude(context, id + "F11", {"entities" : qUnion([Q0]), "operationType" : NewBodyOperationType.ADD, "endBound" : BoundingType.SYMMETRIC, "depth" : 6 * mm});
        }
        {
            var Q0;
            Q0=qCreatedBy(makeId("Right.planeOp"),FACE);
            var sketch = newSketch(context, id + "F12", { "sketchPlane" : qUnion([Q0])});
            skLineSegment(sketch, "E42", {"start": v(-375, 0) * mm, "end": v(-375, 70) * mm});
            skLineSegment(sketch, "E43", {"start": v(-375, 70) * mm, "end": v(-205, 445) * mm});
            skLineSegment(sketch, "E44", {"start": v(-205, 445) * mm, "end": v(205, 445) * mm});
            skLineSegment(sketch, "E45", {"start": v(205, 445) * mm, "end": v(375, 70) * mm});
            skLineSegment(sketch, "E46", {"start": v(375, 70) * mm, "end": v(375, 0) * mm});
            skLineSegment(sketch, "E47", {"start": v(375, 0) * mm, "end": v(-375, 0) * mm});
            skLineSegment(sketch, "E48", {"start": v(0, -2307.15) * mm, "end": v(0, 14569.66) * mm, "construction": true});
            skSolve(sketch);
        }
        {
            var Q0;
            Q0=qSketchRegion(id+"F12",true);
            extrude(context, id + "F13", {"entities" : qUnion([Q0]), "operationType" : NewBodyOperationType.ADD, "endBound" : BoundingType.SYMMETRIC, "depth" : 12 * mm});
        }
        {
            var Q0;
            Q0=qCreatedBy(makeId("Right.planeOp"),FACE);
            cPlane(context, id + "F14", {"entities" : qUnion([Q0]), "cplaneType" : CPlaneType.OFFSET, "offset" : 250 * mm, "width" : 152.4 * mm, "height" : 152.4 * mm});
        }
        {
            var Q0;
            Q0=qCreatedBy(id+"F14.planeOp",FACE);
            var sketch = newSketch(context, id + "F15", { "sketchPlane" : qUnion([Q0])});
            skLineSegment(sketch, "E49", {"start": v(180, 0) * mm, "end": v(180, 445) * mm});
            skLineSegment(sketch, "E50", {"start": v(180, 445) * mm, "end": v(205, 445) * mm});
            skLineSegment(sketch, "E51", {"start": v(205, 445) * mm, "end": v(375, 70) * mm});
            skLineSegment(sketch, "E52", {"start": v(375, 70) * mm, "end": v(375, 0) * mm});
            skLineSegment(sketch, "E53", {"start": v(375, 0) * mm, "end": v(180, 0) * mm});
            skLineSegment(sketch, "E54", {"start": v(0, -1220.16) * mm, "end": v(0, 13301) * mm, "construction": true});
            skLineSegment(sketch, "E55.MirrorCS", {"start": v(-180, 445) * mm, "end": v(-205, 445) * mm});
            skLineSegment(sketch, "E56.MirrorCS", {"start": v(-180, 0) * mm, "end": v(-180, 445) * mm});
            skLineSegment(sketch, "E57.MirrorCS", {"start": v(-205, 445) * mm, "end": v(-375, 70) * mm});
            skLineSegment(sketch, "E58.MirrorCS", {"start": v(-375, 70) * mm, "end": v(-375, 0) * mm});
            skLineSegment(sketch, "E59.MirrorCS", {"start": v(-375, 0) * mm, "end": v(-180, 0) * mm});
            skSolve(sketch);
        }
        {
            var Q0;
            Q0=qSketchRegion(id+"F15",true);
            extrude(context, id + "F16", {"entities" : qUnion([Q0]), "operationType" : NewBodyOperationType.ADD, "endBound" : BoundingType.SYMMETRIC, "depth" : 14 * mm});
        }
        {
            var Q0;
            Q0=qCreatedBy(makeId("Right.planeOp"),FACE);
            cPlane(context, id + "F17", {"entities" : qUnion([Q0]), "cplaneType" : CPlaneType.OFFSET, "offset" : 250 * mm, "oppositeDirection" : true, "width" : 152.4 * mm, "height" : 152.4 * mm});
        }
        {
            var Q0;
            Q0=qCreatedBy(id+"F17.planeOp",FACE);
            var sketch = newSketch(context, id + "F18", { "sketchPlane" : qUnion([Q0])});
            skLineSegment(sketch, "E60", {"start": v(180, 0) * mm, "end": v(180, 445) * mm});
            skLineSegment(sketch, "E61", {"start": v(180, 445) * mm, "end": v(205, 445) * mm});
            skLineSegment(sketch, "E62", {"start": v(205, 445) * mm, "end": v(375, 70) * mm});
            skLineSegment(sketch, "E63", {"start": v(375, 70) * mm, "end": v(375, 0) * mm});
            skLineSegment(sketch, "E64", {"start": v(375, 0) * mm, "end": v(180, 0) * mm});
            skLineSegment(sketch, "E65", {"start": v(0, -106.42) * mm, "end": v(0, 540.56) * mm, "construction": true});
            skLineSegment(sketch, "E66.MirrorCS", {"start": v(-180, 445) * mm, "end": v(-205, 445) * mm});
            skLineSegment(sketch, "E67.MirrorCS", {"start": v(-205, 445) * mm, "end": v(-375, 70) * mm});
            skLineSegment(sketch, "E68.MirrorCS", {"start": v(-180, 0) * mm, "end": v(-180, 445) * mm});
            skLineSegment(sketch, "E69.MirrorCS", {"start": v(-375, 70) * mm, "end": v(-375, 0) * mm});
            skLineSegment(sketch, "E70.MirrorCS", {"start": v(-375, 0) * mm, "end": v(-180, 0) * mm});
            skSolve(sketch);
        }
        {
            var Q0;
            Q0=qSketchRegion(id+"F18",true);
            extrude(context, id + "F19", {"entities" : qUnion([Q0]), "operationType" : NewBodyOperationType.ADD, "endBound" : BoundingType.SYMMETRIC, "depth" : 14 * mm});
        }
        {
            var Q0;
            Q0=qCreatedBy(makeId("Top.planeOp"),FACE);
            var sketch = newSketch(context, id + "F20", { "sketchPlane" : qUnion([Q0])});
            skLineSegment(sketch, "E71", {"start": v(-430, -230) * mm, "end": v(-430, 230) * mm});
            skLineSegment(sketch, "E72", {"start": v(-430, 230) * mm, "end": v(-270, 390) * mm});
            skLineSegment(sketch, "E73", {"start": v(-270, 390) * mm, "end": v(270, 390) * mm});
            skLineSegment(sketch, "E74", {"start": v(270, 390) * mm, "end": v(430, 230) * mm});
            skLineSegment(sketch, "E75", {"start": v(430, 230) * mm, "end": v(430, -230) * mm});
            skLineSegment(sketch, "E76", {"start": v(430, -230) * mm, "end": v(270, -390) * mm});
            skLineSegment(sketch, "E77", {"start": v(270, -390) * mm, "end": v(-270, -390) * mm});
            skLineSegment(sketch, "E78", {"start": v(-270, -390) * mm, "end": v(-430, -230) * mm});
            skLineSegment(sketch, "E79", {"start": v(0, 11047.18) * mm, "end": v(0, -11914.8) * mm, "construction": true});
            skLineSegment(sketch, "E80", {"start": v(-11304.08, 0) * mm, "end": v(12211.2, 0) * mm, "construction": true});
            skCircle(sketch, "E81", {"center": v(170, 290) * mm, "radius": 22 * mm});
            skCircle(sketch, "E82", {"center": v(330, 100) * mm, "radius": 22 * mm});
            skCircle(sketch, "E83.MirrorC", {"center": v(170, -290) * mm, "radius": 22 * mm});
            skCircle(sketch, "E84.MirrorC", {"center": v(330, -100) * mm, "radius": 22 * mm});
            skCircle(sketch, "E85.MirrorC", {"center": v(-170, -290) * mm, "radius": 22 * mm});
            skCircle(sketch, "E86.MirrorC", {"center": v(-170, 290) * mm, "radius": 22 * mm});
            skCircle(sketch, "E87.MirrorC", {"center": v(-330, 100) * mm, "radius": 22 * mm});
            skCircle(sketch, "E88.MirrorC", {"center": v(-330, -100) * mm, "radius": 22 * mm});
            skSolve(sketch);
        }
        {
            var Q0;
            Q0=qSketchRegion(id+"F20",true);
            extrude(context, id + "F21", {"entities" : qUnion([Q0]), "operationType" : NewBodyOperationType.ADD, "depth" : 45 * mm});
        }
        {
            var Q0;
            Q0=qCreatedBy(makeId("Top.planeOp"),FACE);
            cPlane(context, id + "F22", {"entities" : qUnion([Q0]), "cplaneType" : CPlaneType.OFFSET, "offset" : 11250 * mm, "width" : 152.4 * mm, "height" : 152.4 * mm});
        }
        {
            var Q0;
            Q0=qCreatedBy(id+"F22.planeOp",FACE);
            var sketch = newSketch(context, id + "F23", { "sketchPlane" : qUnion([Q0])});
            skLineSegment(sketch, "E89", {"start": v(0, 9266.93) * mm, "end": v(0, -9722.2) * mm, "construction": true});
            skLineSegment(sketch, "E90", {"start": v(-26607.47, 0) * mm, "end": v(25005.8, 0) * mm, "construction": true});
            skLineSegment(sketch, "E91.bottom", {"start": v(254, 167.3) * mm, "end": v(425, 167.3) * mm});
            skLineSegment(sketch, "E91.top", {"start": v(254, -167.3) * mm, "end": v(425, -167.3) * mm});
            skLineSegment(sketch, "E91.left", {"start": v(254, 167.3) * mm, "end": v(254, -167.3) * mm});
            skLineSegment(sketch, "E91.right", {"start": v(425, 167.3) * mm, "end": v(425, -167.3) * mm});
            skSolve(sketch);
        }
        {
            var Q0;
            Q0=qSketchRegion(id+"F23",true);
            extrude(context, id + "F24", {"entities" : qUnion([Q0]), "operationType" : NewBodyOperationType.ADD, "endBound" : BoundingType.SYMMETRIC, "depth" : 10 * mm});
        }
    });
